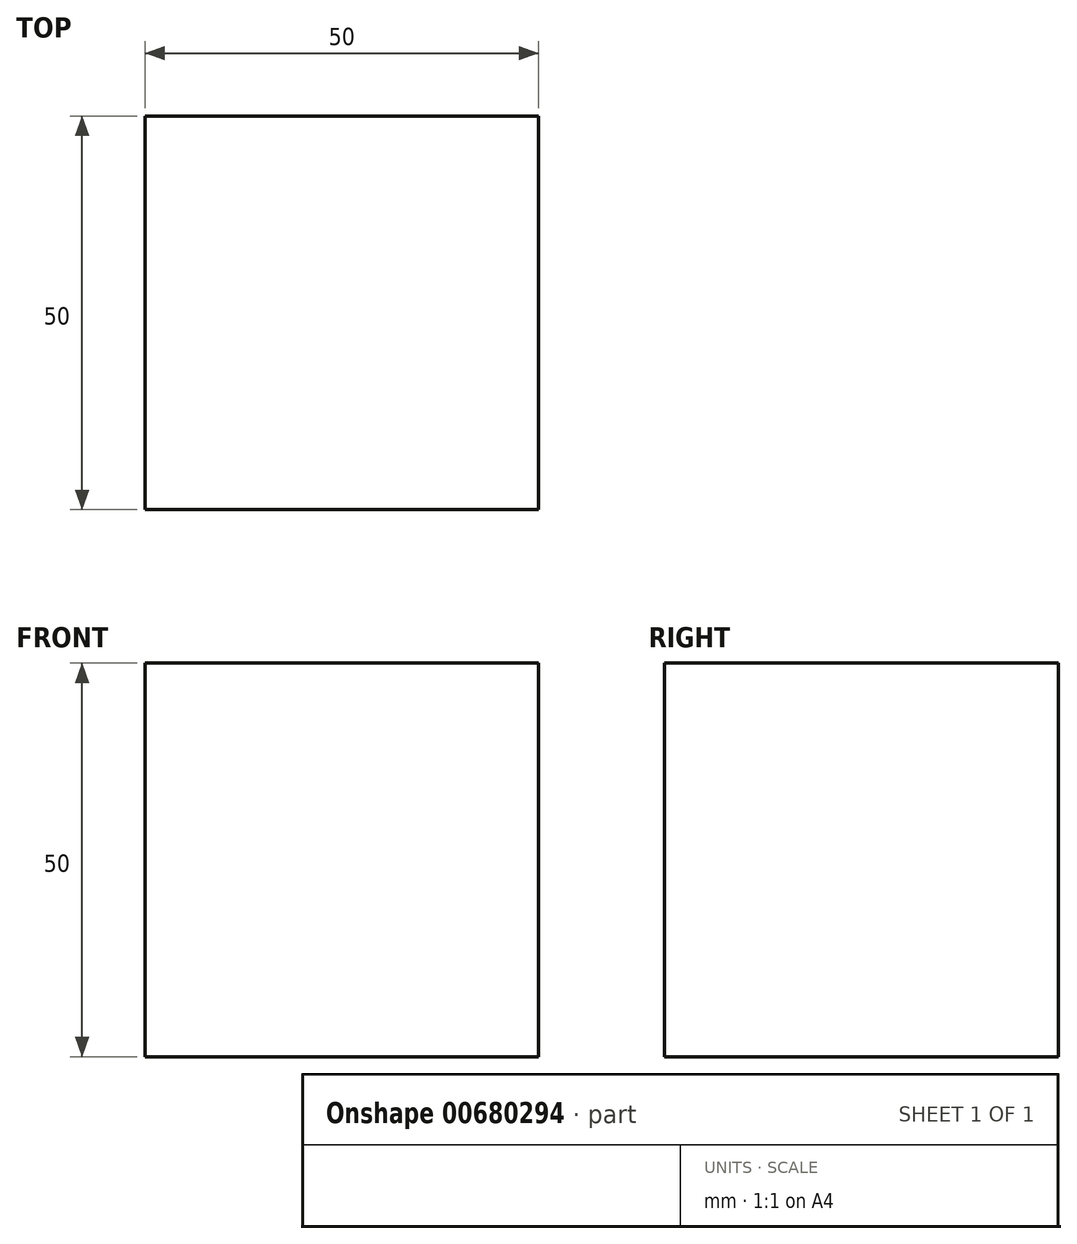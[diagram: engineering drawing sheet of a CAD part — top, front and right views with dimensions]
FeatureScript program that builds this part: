
annotation { "Feature Type Name" : "Feature", "Feature Type Description" : "" }
export const myFeature = defineFeature(function(context is Context, id is Id, definition is map)
    precondition{}
    {
        {
            var Q0;
            Q0=qCreatedBy(makeId("Top.planeOp"),FACE);
            var sketch = newSketch(context, id + "F0", { "sketchPlane" : qUnion([Q0])});
            skLineSegment(sketch, "E0.bottom", {"start": v(-15.07, 15.2) * mm, "end": v(34.93, 15.2) * mm});
            skLineSegment(sketch, "E0.top", {"start": v(-15.07, -34.8) * mm, "end": v(34.93, -34.8) * mm});
            skLineSegment(sketch, "E0.left", {"start": v(-15.07, 15.2) * mm, "end": v(-15.07, -34.8) * mm});
            skLineSegment(sketch, "E0.right", {"start": v(34.93, 15.2) * mm, "end": v(34.93, -34.8) * mm});
            skSolve(sketch);
        }
        {
            var Q0;
            Q0 = qSketchRegion(id + "F0", true);
            extrude(context, id + "F1", {"entities" : qUnion([Q0]), "depth" : 50 * mm, "offsetDistance" : 25 * mm});
        }
    });
